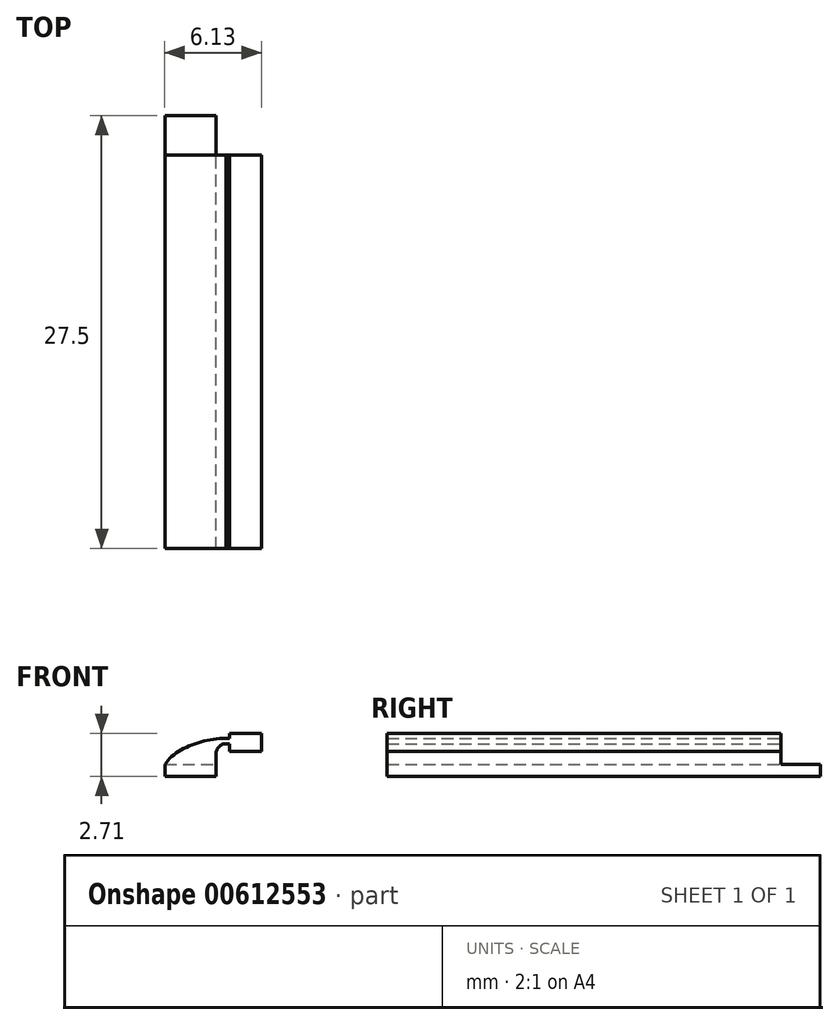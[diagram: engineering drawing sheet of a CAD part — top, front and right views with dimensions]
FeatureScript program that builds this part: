
annotation { "Feature Type Name" : "Feature", "Feature Type Description" : "" }
export const myFeature = defineFeature(function(context is Context, id is Id, definition is map)
    precondition{}
    {
        {
            var Q0;
            Q0=qCreatedBy(makeId("Front.planeOp"),FACE);
            var sketch = newSketch(context, id + "F0", { "sketchPlane" : qUnion([Q0])});
            skLineSegment(sketch, "E0.bottom", {"start": v(-1.63, 0.37) * mm, "end": v(1.62, 0.38) * mm});
            skLineSegment(sketch, "E0.top", {"start": v(-1.63, -0.38) * mm, "end": v(1.63, -0.38) * mm});
            skLineSegment(sketch, "E0.left", {"start": v(-1.63, 0.37) * mm, "end": v(-1.63, -0.38) * mm});
            skLineSegment(sketch, "E0.right", {"start": v(1.62, 0.38) * mm, "end": v(1.63, -0.37) * mm});
            skPoint(sketch, "E0.middle", {"position": v(0, 0) * mm});
            skLineSegment(sketch, "E1.bottom", {"start": v(4.5, 2.33) * mm, "end": v(2.5, 2.33) * mm});
            skLineSegment(sketch, "E1.top", {"start": v(4.5, 1.2) * mm, "end": v(2.5, 1.2) * mm});
            skLineSegment(sketch, "E1.left", {"start": v(4.5, 2.33) * mm, "end": v(4.5, 1.2) * mm});
            skLineSegment(sketch, "E1.right", {"start": v(2.5, 2.33) * mm, "end": v(2.5, 1.2) * mm});
            skLineSegment(sketch, "E2", {"start": v(1.62, 0.38) * mm, "end": v(1.62, 1.04) * mm});
            skArc(sketch, "E3", {"start": v(2.27, 1.69) * mm, "mid": v(1.82, 1.5) * mm, "end": v(1.62, 1.04) * mm});
            skLineSegment(sketch, "E4", {"start": v(2.27, 1.69) * mm, "end": v(3.35, 1.69) * mm});
            skLineSegment(sketch, "E5.0", {"start": v(2.27, 2.04) * mm, "end": v(3.35, 2.04) * mm});
            skArc(sketch, "E5.1", {"start": v(2.27, 2.04) * mm, "mid": v(1.57, 1.75) * mm, "end": v(1.27, 1.04) * mm});
            skLineSegment(sketch, "E5.2", {"start": v(1.27, 0.38) * mm, "end": v(1.27, 1.04) * mm});
            skLineSegment(sketch, "E6", {"start": v(3.35, 2.04) * mm, "end": v(3.35, 1.69) * mm});
            skFitSpline(sketch, "E7", {"points": [v(-1.63, 0.37) * mm, v(2.27, 2.04) * mm], "startDerivative": vector(2.03, 3.08) * mm, "endDerivative": vector(4.48, 0.05) * mm});
            skSolve(sketch);
        }
        {
            var Q0;
            Q0=makeQuery(id+"F0.imprint","IMPRINT",FACE,{"disambiguationData":[TD([[makeQuery(id+"F0.imprint","IMPRINT",EDGE,{"derivedFrom":sQuery(id+"F0.wireOp",EDGE,"E0.top")}),1.0]])]});
            extrude(context, id + "F1", {"entities" : qUnion([Q0]), "endBound" : BoundingType.SYMMETRIC, "depth" : 5 * mm, "offsetDistance" : 25 * mm});
        }
        {
            var Q0;
            Q0 = qSketchRegion(id + "F0", true);
            extrude(context, id + "F2", {"entities" : qUnion([Q0]), "operationType" : NewBodyOperationType.ADD, "depth" : 25 * mm, "offsetDistance" : 25 * mm});
        }
    });
